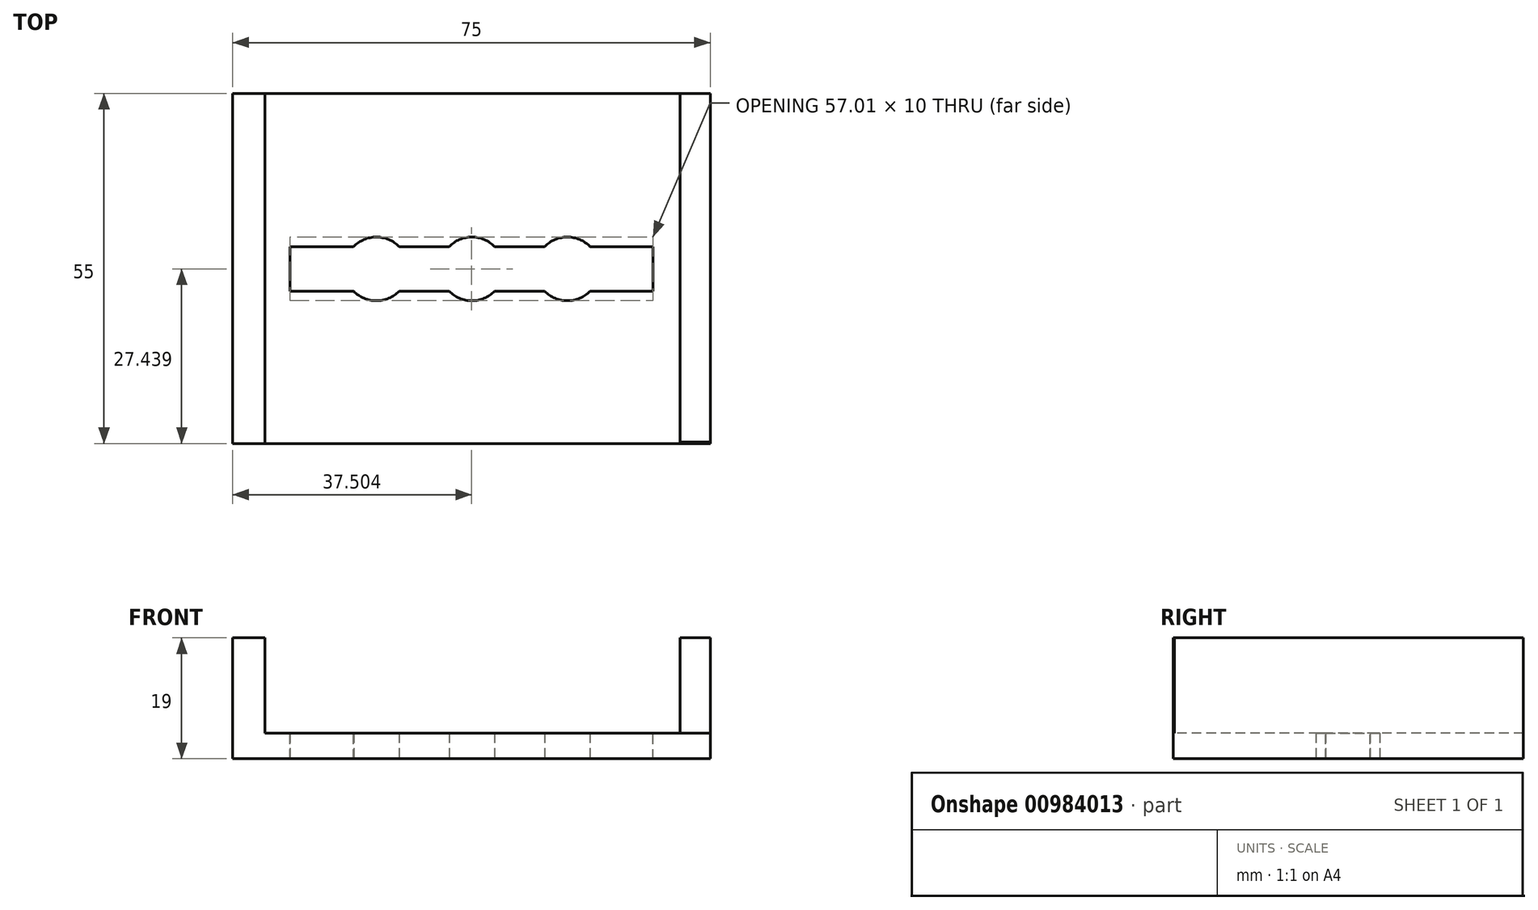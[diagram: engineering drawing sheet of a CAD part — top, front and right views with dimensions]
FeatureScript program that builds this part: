
annotation { "Feature Type Name" : "Feature", "Feature Type Description" : "" }
export const myFeature = defineFeature(function(context is Context, id is Id, definition is map)
    precondition{}
    {
        {
            var Q0;
            Q0=qCreatedBy(makeId("Top.planeOp"),FACE);
            var sketch = newSketch(context, id + "F0", { "sketchPlane" : qUnion([Q0])});
            skLineSegment(sketch, "E0.bottom", {"start": v(-60.33, 2.74) * mm, "end": v(14.67, 2.74) * mm});
            skLineSegment(sketch, "E0.top", {"start": v(-60.33, -52.26) * mm, "end": v(14.67, -52.26) * mm});
            skLineSegment(sketch, "E0.left", {"start": v(-60.33, 2.74) * mm, "end": v(-60.33, -52.26) * mm});
            skLineSegment(sketch, "E0.right", {"start": v(14.67, 2.74) * mm, "end": v(14.67, -52.26) * mm});
            skSolve(sketch);
        }
        {
            var Q0;
            Q0=makeQuery(id+"F0.imprint","IMPRINT",FACE,{"disambiguationData":[TD([[makeQuery(id+"F0.imprint","IMPRINT",EDGE,{"derivedFrom":sQuery(id+"F0.wireOp",EDGE,"E0.bottom")}),-1.0]])]});
            var sketch = newSketch(context, id + "F1", { "sketchPlane" : qUnion([Q0])});
            skSolve(sketch);
        }
        {
            var Q0;
            Q0=makeQuery(id+"F0.imprint","IMPRINT",FACE,{"disambiguationData":[TD([[makeQuery(id+"F0.imprint","IMPRINT",EDGE,{"derivedFrom":sQuery(id+"F0.wireOp",EDGE,"E0.bottom")}),-1.0]])]});
            extrude(context, id + "F2", {"entities" : qUnion([Q0]), "depth" : 4 * mm, "offsetDistance" : 25 * mm});
        }
        {
            var Q0;
            Q0=makeQuery(id+"F2.opExtrude","CAP_FACE",FACE,{"disambiguationData":[OSD([sQuery(id+"F0.wireOp",EDGE,"E0.bottom"),sQuery(id+"F0.wireOp",EDGE,"E0.top"),sQuery(id+"F0.wireOp",EDGE,"E0.left"),sQuery(id+"F0.wireOp",EDGE,"E0.right")])],"isStart":false});
            var sketch = newSketch(context, id + "F3", { "sketchPlane" : qUnion([Q0])});
            skLineSegment(sketch, "E1", {"start": v(-60.33, -52.26) * mm, "end": v(-55.33, -52.26) * mm});
            skSolve(sketch);
        }
        {
            var Q0;
            {var subQ2=sQuery(id+"F3.wireOp",EDGE,"E1");Q0=makeQuery(id+"F3.imprint","IMPRINT",FACE,{"disambiguationData":[TD([[makeQuery(id+"F3.imprint","IMPRINT",EDGE,{"derivedFrom":subQ2}),1.0]])]});}
            var sketch = newSketch(context, id + "F4", { "sketchPlane" : qUnion([Q0])});
            skLineSegment(sketch, "E2", {"start": v(-55.26, -52.38) * mm, "end": v(-55.26, 3.05) * mm});
            skLineSegment(sketch, "E3", {"start": v(-60.49, 2.83) * mm, "end": v(-55.26, 2.83) * mm});
            skSolve(sketch);
        }
        {
            var Q0;
            {var subQ4=sQuery(id+"F3.wireOp",EDGE,"E1");var subQ5=makeQuery(id+"F3.imprint","IMPRINT",EDGE,{"derivedFrom":subQ4});Q0=makeQuery(id+"F4.imprint","IMPRINT",FACE,{"disambiguationData":[TD([[makeQuery(id+"F4.imprint","IMPRINT",EDGE,{"derivedFrom":subQ5}),1.0]])]});}
            extrude(context, id + "F5", {"entities" : qUnion([Q0]), "operationType" : NewBodyOperationType.ADD, "depth" : 15 * mm, "offsetDistance" : 25 * mm});
        }
        {
            var Q0;
            {var subQ2=sQuery(id+"F3.wireOp",EDGE,"E1");Q0=makeQuery(id+"F3.imprint","IMPRINT",FACE,{"disambiguationData":[TD([[makeQuery(id+"F3.imprint","IMPRINT",EDGE,{"derivedFrom":subQ2}),1.0]])]});}
            var sketch = newSketch(context, id + "F6", { "sketchPlane" : qUnion([Q0])});
            skLineSegment(sketch, "E4", {"start": v(14.93, 2.75) * mm, "end": v(9.93, 2.75) * mm});
            skLineSegment(sketch, "E5", {"start": v(9.93, 2.75) * mm, "end": v(9.93, -52.04) * mm});
            skLineSegment(sketch, "E6", {"start": v(9.93, -52.04) * mm, "end": v(14.93, -52.04) * mm});
            skLineSegment(sketch, "E7", {"start": v(14.93, -52.04) * mm, "end": v(14.93, 2.75) * mm});
            skSolve(sketch);
        }
        {
            var Q0;
            {var subQ0=sQuery(id+"F6.wireOp",EDGE,"E6");var subQ1=sQuery(id+"F6.wireOp",EDGE,"E5");var subQ2=makeQuery(id+"F6.imprint","INTERSECT",VERTEX,{"derivedFrom":[subQ1,subQ0]});Q0=makeQuery(id+"F6.imprint","IMPRINT",FACE,{"disambiguationData":[TD([[makeQuery(id+"F6.imprint","IMPRINT",EDGE,{"disambiguationData":[TD([[subQ2,1.0]])],"derivedFrom":subQ1}),1.0]])]});}
            extrude(context, id + "F7", {"entities" : qUnion([Q0]), "operationType" : NewBodyOperationType.ADD, "depth" : 15 * mm, "offsetDistance" : 25 * mm});
        }
        {
            var Q0;
            Q0=makeQuery(id+"F1.imprint","IMPRINT",FACE,{"disambiguationData":[TD([[makeQuery(id+"F1.imprint","IMPRINT",EDGE,{"derivedFrom":makeQuery(id+"F0.imprint","IMPRINT",EDGE,{"derivedFrom":sQuery(id+"F0.wireOp",EDGE,"E0.bottom")})}),-1.0]])]});
            var sketch = newSketch(context, id + "F8", { "sketchPlane" : qUnion([Q0])});
            skPoint(sketch, "E8", {"position": v(-60.29, -52.32) * mm});
            skPoint(sketch, "E9", {"position": v(-60.25, 2.68) * mm});
            skLineSegment(sketch, "E10", {"start": v(-60.29, -52.32) * mm, "end": v(-60.25, 2.68) * mm});
            skLineSegment(sketch, "E11", {"start": v(-60.29, -52.32) * mm, "end": v(-60.27, -24.82) * mm});
            skLineSegment(sketch, "E12", {"start": v(-60.27, -24.82) * mm, "end": v(14.73, -24.82) * mm});
            skLineSegment(sketch, "E13", {"start": v(14.73, -24.82) * mm, "end": v(14.71, -52.32) * mm});
            skLineSegment(sketch, "E14", {"start": v(14.71, -52.32) * mm, "end": v(14.73, -24.82) * mm});
            skLineSegment(sketch, "E15", {"start": v(14.73, 2.59) * mm, "end": v(14.73, -24.82) * mm});
            skPoint(sketch, "E16", {"position": v(-22.77, -24.82) * mm});
            skCircle(sketch, "E17", {"center": v(-22.77, -24.82) * mm, "radius": 5 * mm});
            skLineSegment(sketch, "E18", {"start": v(-17.77, -24.82) * mm, "end": v(-7.77, -24.82) * mm});
            skCircle(sketch, "E19", {"center": v(-7.77, -24.82) * mm, "radius": 5 * mm});
            skLineSegment(sketch, "E20", {"start": v(-27.77, -24.82) * mm, "end": v(-37.77, -24.82) * mm});
            skCircle(sketch, "E21", {"center": v(-37.77, -24.82) * mm, "radius": 5 * mm});
            skSolve(sketch);
        }
        {
            var Q0;
            Q0=sQuery(id+"F8.wireOp",VERTEX,"E20.end");
            var Q1;
            Q1=sQuery(id+"F8.wireOp",VERTEX,"E16");
            var Q2;
            Q2=sQuery(id+"F8.wireOp",VERTEX,"E18.end");
            var Q3;
            Q3=makeQuery(id+"F2.opExtrude","SWEPT_BODY",BODY,{"disambiguationData":[OSD([sQuery(id+"F0.wireOp",EDGE,"E0.bottom"),sQuery(id+"F0.wireOp",EDGE,"E0.top"),sQuery(id+"F0.wireOp",EDGE,"E0.left"),sQuery(id+"F0.wireOp",EDGE,"E0.right")])]});
            hole(context, id + "F9", {"style" : HoleStyle.SIMPLE, "endStyle" : HoleEndStyle.THROUGH, "oppositeDirection" : true, "holeDiameter" : 10 * mm, "majorDiameter" : 5 * mm, "isTappedThrough" : true, "tappedDepth" : 12 * mm, "tapClearance" : 3, "locations" : qUnion([Q0, Q1, Q2]), "scope" : qUnion([Q3])});
        }
        {
            var Q0;
            Q0=makeQuery(id+"F1.imprint","IMPRINT",FACE,{"disambiguationData":[TD([[makeQuery(id+"F1.imprint","IMPRINT",EDGE,{"derivedFrom":makeQuery(id+"F0.imprint","IMPRINT",EDGE,{"derivedFrom":sQuery(id+"F0.wireOp",EDGE,"E0.bottom")})}),-1.0]])]});
            var sketch = newSketch(context, id + "F10", { "sketchPlane" : qUnion([Q0])});
            skLineSegment(sketch, "E22", {"start": v(-41.33, -28.32) * mm, "end": v(-41.33, -21.32) * mm});
            skLineSegment(sketch, "E23", {"start": v(-41.33, -28.32) * mm, "end": v(-51.32, -28.32) * mm});
            skLineSegment(sketch, "E24", {"start": v(-41.33, -21.32) * mm, "end": v(-51.33, -21.32) * mm});
            skLineSegment(sketch, "E25", {"start": v(-51.33, -21.32) * mm, "end": v(-51.32, -28.32) * mm});
            skSolve(sketch);
        }
        {
            var Q0;
            Q0=makeQuery(id+"F10.imprint","IMPRINT",FACE,{"disambiguationData":[TD([[makeQuery(id+"F10.imprint","IMPRINT",EDGE,{"derivedFrom":sQuery(id+"F10.wireOp",EDGE,"E22")}),1.0]])]});
            extrude(context, id + "F11", {"entities" : qUnion([Q0]), "operationType" : NewBodyOperationType.REMOVE, "depth" : 10 * mm, "offsetDistance" : 25 * mm});
        }
        {
            var Q0;
            {var subQ2=sQuery(id+"F3.wireOp",EDGE,"E1");Q0=makeQuery(id+"F3.imprint","IMPRINT",FACE,{"disambiguationData":[TD([[makeQuery(id+"F3.imprint","IMPRINT",EDGE,{"derivedFrom":subQ2}),1.0]])]});}
            var sketch = newSketch(context, id + "F12", { "sketchPlane" : qUnion([Q0])});
            skPoint(sketch, "E26", {"position": v(-51.33, -21.32) * mm});
            skPoint(sketch, "E27", {"position": v(-51.32, -28.32) * mm});
            skLineSegment(sketch, "E28", {"start": v(-51.33, -21.32) * mm, "end": v(5.67, -21.32) * mm});
            skLineSegment(sketch, "E29", {"start": v(-51.32, -28.32) * mm, "end": v(5.68, -28.32) * mm});
            skLineSegment(sketch, "E30", {"start": v(5.68, -28.32) * mm, "end": v(5.67, -21.32) * mm});
            skLineSegment(sketch, "E31", {"start": v(-51.32, -28.32) * mm, "end": v(-51.33, -21.32) * mm});
            skSolve(sketch);
        }
        {
            var Q0;
            Q0=makeQuery(id+"F12.imprint","IMPRINT",FACE,{"disambiguationData":[TD([[makeQuery(id+"F12.imprint","IMPRINT",EDGE,{"derivedFrom":sQuery(id+"F12.wireOp",EDGE,"E28")}),-1.0]])]});
            extrude(context, id + "F13", {"entities" : qUnion([Q0]), "operationType" : NewBodyOperationType.REMOVE, "oppositeDirection" : true, "depth" : 100 * mm, "offsetDistance" : 25 * mm});
        }
    });
